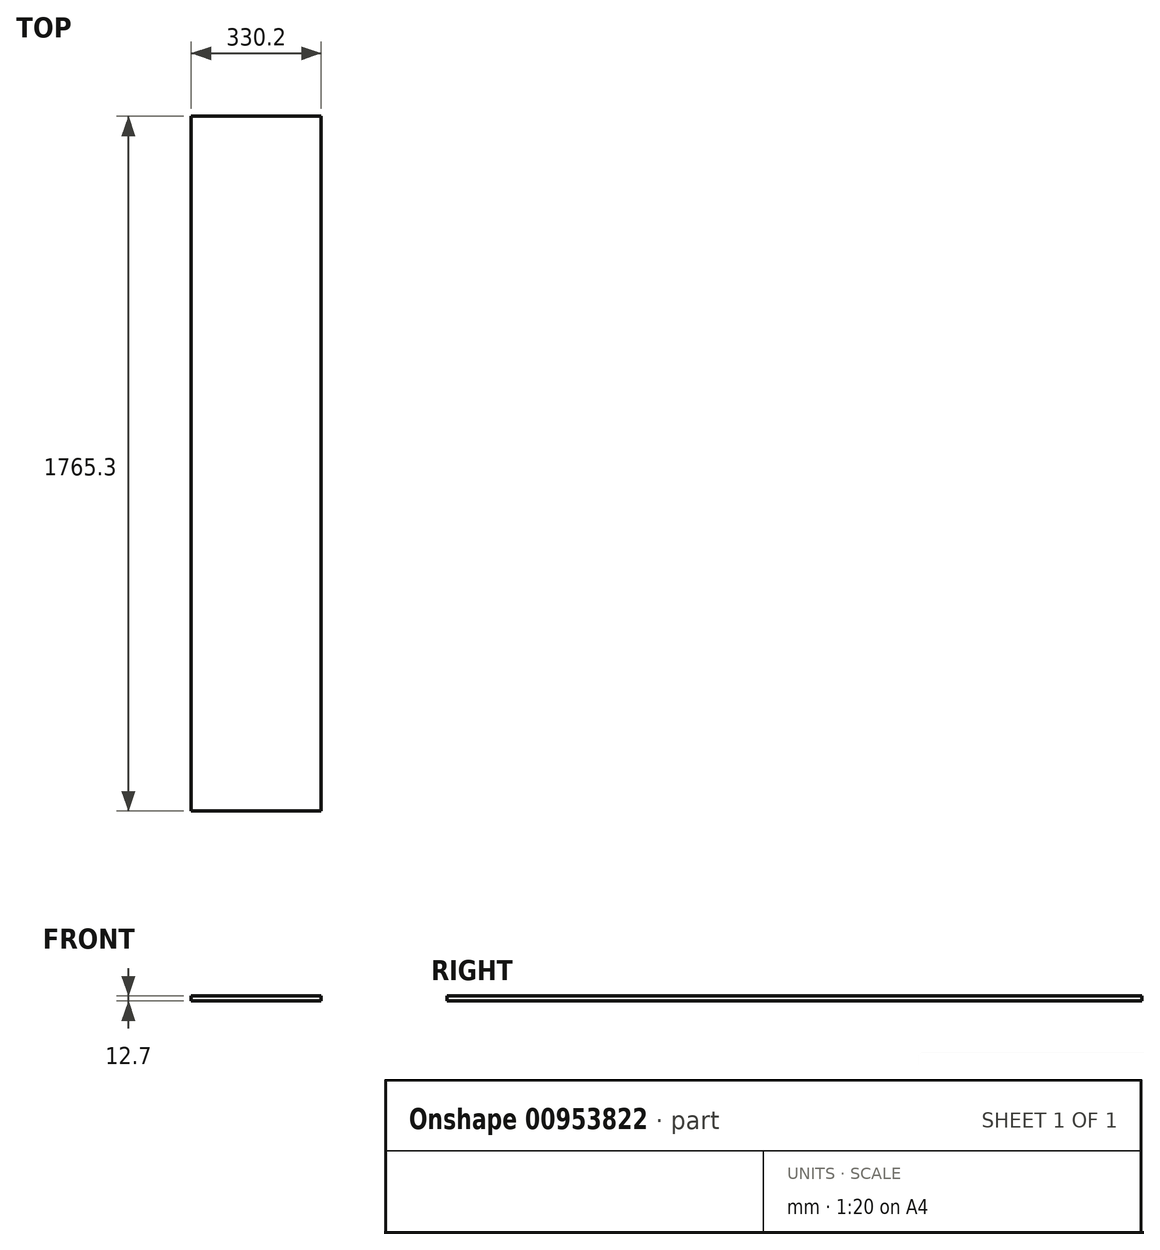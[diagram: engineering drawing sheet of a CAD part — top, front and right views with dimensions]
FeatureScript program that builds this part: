
annotation { "Feature Type Name" : "Feature", "Feature Type Description" : "" }
export const myFeature = defineFeature(function(context is Context, id is Id, definition is map)
    precondition{}
    {
        {
            var Q0;
            Q0=qCreatedBy(makeId("Front.planeOp"),FACE);
            var sketch = newSketch(context, id + "F0", { "sketchPlane" : qUnion([Q0])});
            skLineSegment(sketch, "E0.bottom", {"start": v(-165.1, -6.35) * mm, "end": v(165.1, -6.35) * mm});
            skLineSegment(sketch, "E0.top", {"start": v(-165.1, 6.35) * mm, "end": v(165.1, 6.35) * mm});
            skLineSegment(sketch, "E0.left", {"start": v(-165.1, -6.35) * mm, "end": v(-165.1, 6.35) * mm});
            skLineSegment(sketch, "E0.right", {"start": v(165.1, -6.35) * mm, "end": v(165.1, 6.35) * mm});
            skPoint(sketch, "E0.middle", {"position": v(0, 0) * mm});
            skSolve(sketch);
        }
        {
            var Q0;
            Q0 = qSketchRegion(id + "F0", true);
            extrude(context, id + "F1", {"entities" : qUnion([Q0]), "depth" : 1765.3 * mm, "offsetDistance" : 25.4 * mm});
        }
    });
